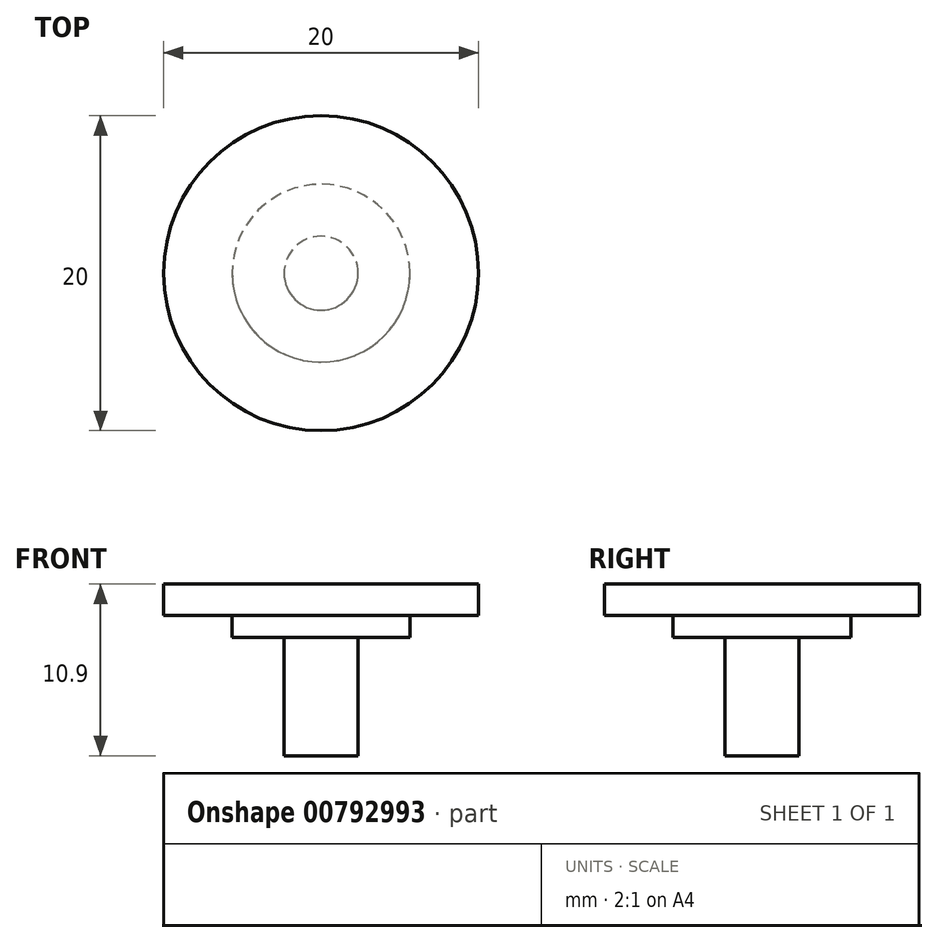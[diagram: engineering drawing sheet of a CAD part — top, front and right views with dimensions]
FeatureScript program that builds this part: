
annotation { "Feature Type Name" : "Feature", "Feature Type Description" : "" }
export const myFeature = defineFeature(function(context is Context, id is Id, definition is map)
    precondition{}
    {
        {
            var Q0;
            Q0=qCreatedBy(makeId("Top.planeOp"),FACE);
            var sketch = newSketch(context, id + "F0", { "sketchPlane" : qUnion([Q0])});
            skCircle(sketch, "E0", {"center": v(0, 0) * mm, "radius": 2.35 * mm});
            skSolve(sketch);
        }
        {
            var Q0;
            Q0=qSketchRegion(id+"F0",true);
            extrude(context, id + "F1", {"entities" : qUnion([Q0]), "depth" : 7.5 * mm, "offsetDistance" : 25 * mm});
        }
        {
            var Q0;
            Q0=makeQuery(id+"F1.opExtrude","CAP_FACE",FACE,{"disambiguationData":[OSD([sQuery(id+"F0.wireOp",EDGE,"E0")])],"isStart":false});
            var sketch = newSketch(context, id + "F2", { "sketchPlane" : qUnion([Q0])});
            skCircle(sketch, "E1", {"center": v(0, 0) * mm, "radius": 10 * mm});
            skSolve(sketch);
        }
        {
            var Q0;
            Q0=qSketchRegion(id+"F2",true);
            extrude(context, id + "F3", {"entities" : qUnion([Q0]), "operationType" : NewBodyOperationType.ADD, "depth" : 2 * mm, "offsetDistance" : 25 * mm});
        }
        {
            var Q0;
            Q0=makeQuery(id+"F3.opExtrude","CAP_FACE",FACE,{"disambiguationData":[OSD([sQuery(id+"F2.wireOp",EDGE,"E1")])],"isStart":true});
            var sketch = newSketch(context, id + "F4", { "sketchPlane" : qUnion([Q0])});
            skCircle(sketch, "E2", {"center": v(0, 0) * mm, "radius": 5.65 * mm});
            skSolve(sketch);
        }
        {
            var Q0;
            Q0 = qSketchRegion(id + "F4", true);
            var Q1;
            Q1=makeQuery(id+"F1.opExtrude","CAP_FACE",FACE,{"disambiguationData":[OSD([sQuery(id+"F0.wireOp",EDGE,"E0")])],"isStart":true});
            extrude(context, id + "F5", {"entities" : qUnion([Q0, Q1]), "operationType" : NewBodyOperationType.ADD, "depth" : 1.4 * mm, "offsetDistance" : 25 * mm});
        }
    });
